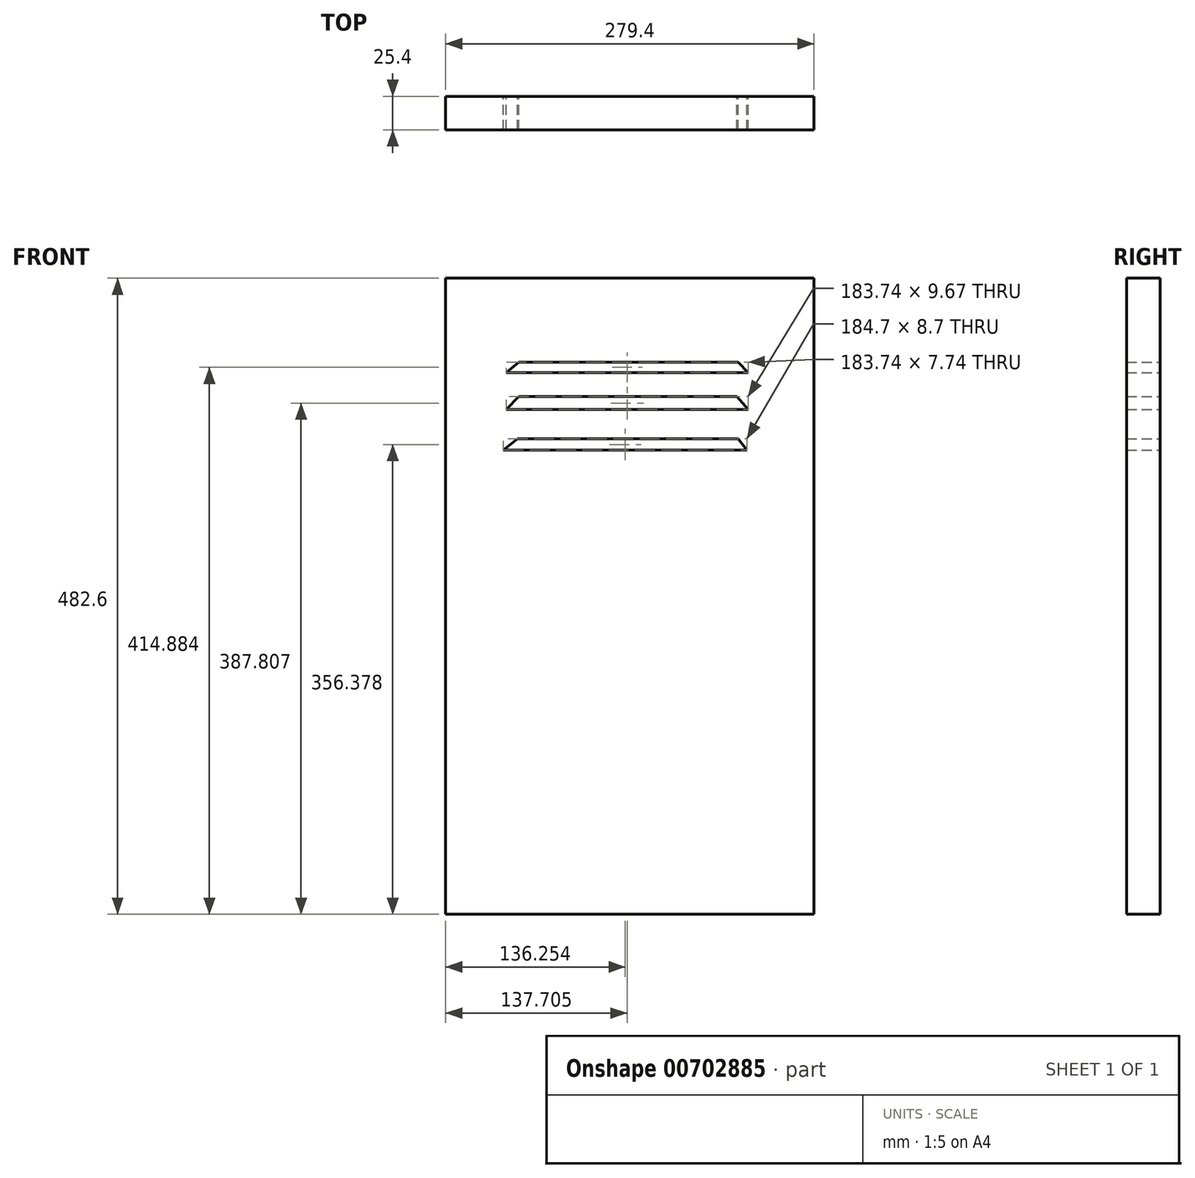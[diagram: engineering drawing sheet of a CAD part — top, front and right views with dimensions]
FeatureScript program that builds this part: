
annotation { "Feature Type Name" : "Feature", "Feature Type Description" : "" }
export const myFeature = defineFeature(function(context is Context, id is Id, definition is map)
    precondition{}
    {
        {
            var Q0;
            Q0=qCreatedBy(makeId("Front.planeOp"),FACE);
            var sketch = newSketch(context, id + "F0", { "sketchPlane" : qUnion([Q0])});
            skLineSegment(sketch, "E0.bottom", {"start": v(-139.7, -241.3) * mm, "end": v(139.7, -241.3) * mm});
            skLineSegment(sketch, "E0.top", {"start": v(-139.7, 241.3) * mm, "end": v(139.7, 241.3) * mm});
            skLineSegment(sketch, "E0.left", {"start": v(-139.7, -241.3) * mm, "end": v(-139.7, 241.3) * mm});
            skLineSegment(sketch, "E0.right", {"start": v(139.7, -241.3) * mm, "end": v(139.7, 241.3) * mm});
            skPoint(sketch, "E0.middle", {"position": v(0, 0) * mm});
            skLineSegment(sketch, "E1", {"start": v(-84.2, 177.45) * mm, "end": v(82.14, 177.45) * mm});
            skLineSegment(sketch, "E2", {"start": v(89.87, 169.72) * mm, "end": v(82.14, 177.45) * mm});
            skLineSegment(sketch, "E3", {"start": v(-84.2, 177.45) * mm, "end": v(-93.86, 169.72) * mm});
            skLineSegment(sketch, "E4", {"start": v(-93.86, 169.72) * mm, "end": v(89.87, 169.72) * mm});
            skLineSegment(sketch, "E5", {"start": v(-84.2, 151.34) * mm, "end": v(-93.86, 141.67) * mm});
            skLineSegment(sketch, "E6", {"start": v(-93.86, 141.67) * mm, "end": v(89.87, 141.67) * mm});
            skLineSegment(sketch, "E7", {"start": v(89.87, 141.67) * mm, "end": v(81.17, 151.34) * mm});
            skLineSegment(sketch, "E8", {"start": v(81.17, 151.34) * mm, "end": v(-84.2, 151.34) * mm});
            skLineSegment(sketch, "E9", {"start": v(-85.16, 119.43) * mm, "end": v(82.14, 119.43) * mm});
            skLineSegment(sketch, "E10", {"start": v(82.14, 119.43) * mm, "end": v(88.9, 110.73) * mm});
            skLineSegment(sketch, "E11", {"start": v(88.9, 110.73) * mm, "end": v(-95.8, 110.73) * mm});
            skLineSegment(sketch, "E12", {"start": v(-95.8, 110.73) * mm, "end": v(-85.16, 119.43) * mm});
            skSolve(sketch);
        }
        {
            var Q0;
            Q0=makeQuery(id+"F0.imprint","IMPRINT",FACE,{"disambiguationData":[TD([[makeQuery(id+"F0.imprint","IMPRINT",EDGE,{"derivedFrom":sQuery(id+"F0.wireOp",EDGE,"E0.bottom")}),1.0]])]});
            extrude(context, id + "F1", {"entities" : qUnion([Q0]), "depth" : 25.4 * mm, "offsetDistance" : 25.4 * mm});
        }
    });
